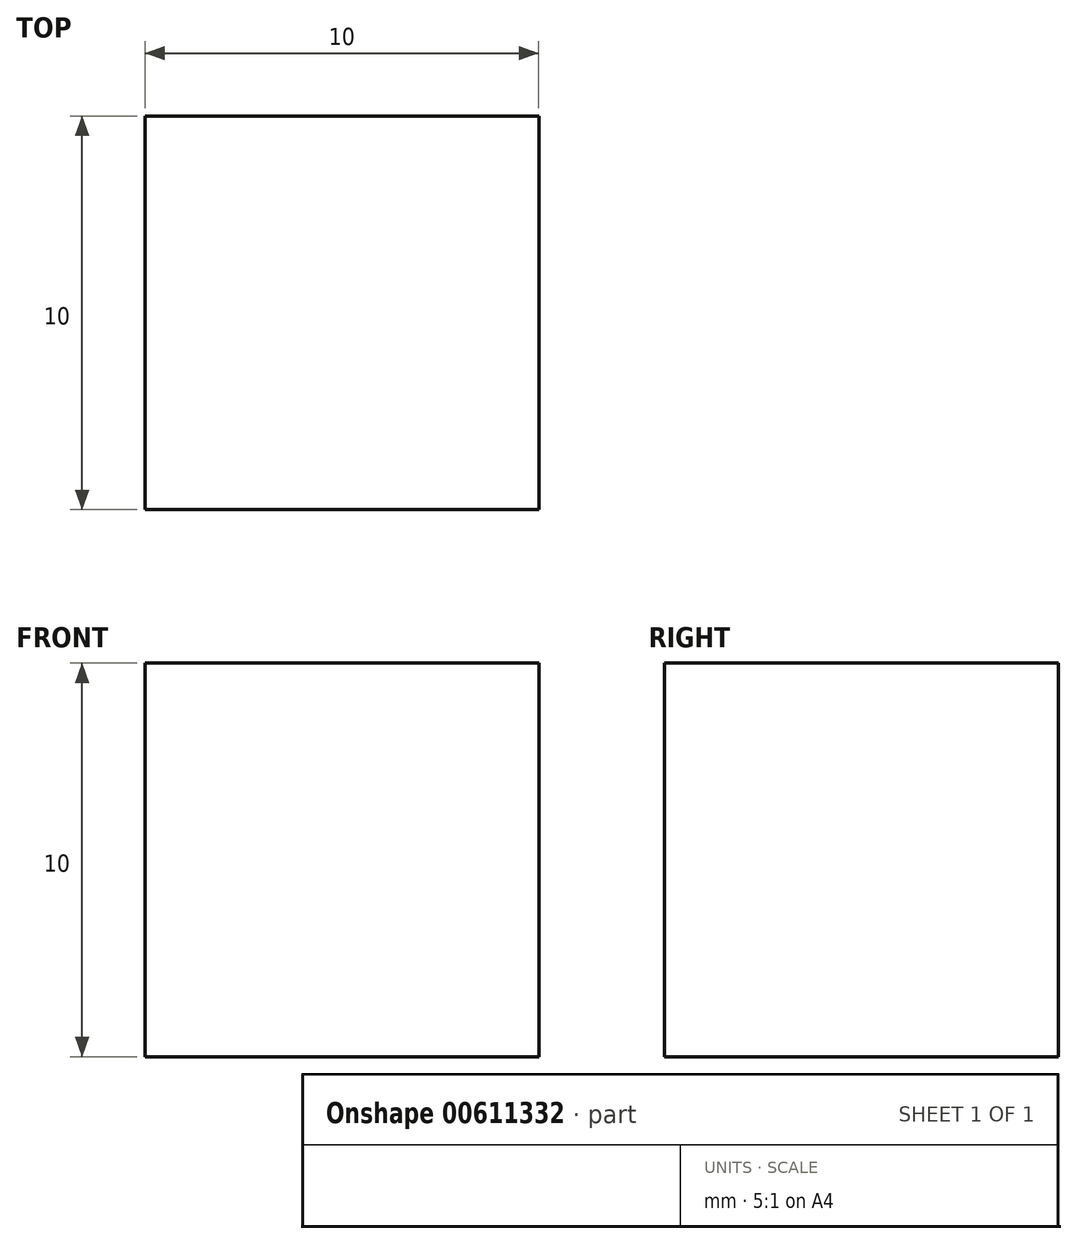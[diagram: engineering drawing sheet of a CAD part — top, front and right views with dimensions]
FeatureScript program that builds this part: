
annotation { "Feature Type Name" : "Feature", "Feature Type Description" : "" }
export const myFeature = defineFeature(function(context is Context, id is Id, definition is map)
    precondition{}
    {
        {
            var Q0;
            Q0=qCreatedBy(makeId("Front.planeOp"),FACE);
            var sketch = newSketch(context, id + "F0", { "sketchPlane" : qUnion([Q0])});
            skLineSegment(sketch, "E0.bottom", {"start": v(-28.75, 21.14) * mm, "end": v(-18.75, 21.14) * mm});
            skLineSegment(sketch, "E0.top", {"start": v(-28.75, 11.14) * mm, "end": v(-18.75, 11.14) * mm});
            skLineSegment(sketch, "E0.left", {"start": v(-28.75, 21.14) * mm, "end": v(-28.75, 11.14) * mm});
            skLineSegment(sketch, "E0.right", {"start": v(-18.75, 21.14) * mm, "end": v(-18.75, 11.14) * mm});
            skSolve(sketch);
        }
        {
            var Q0;
            Q0 = qSketchRegion(id + "F0", true);
            extrude(context, id + "F1", {"entities" : qUnion([Q0]), "depth" : 10 * mm, "offsetDistance" : 25 * mm});
        }
    });
